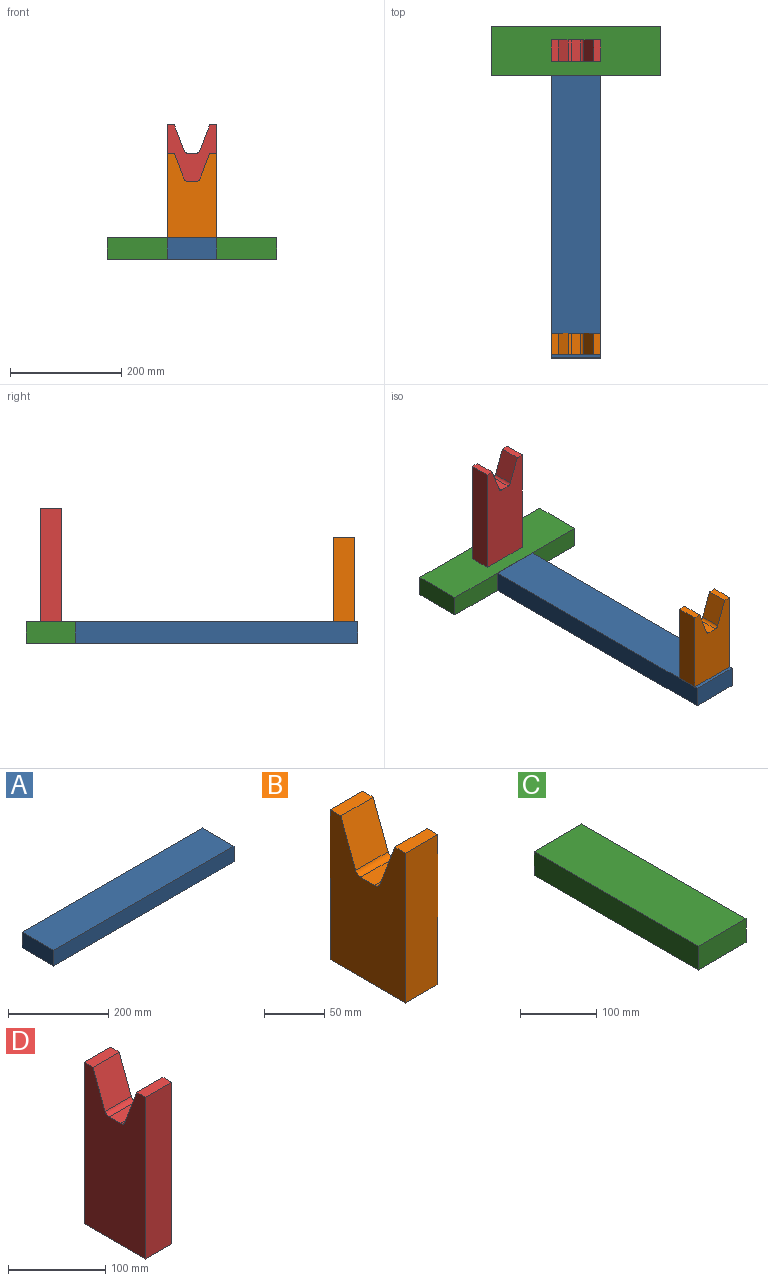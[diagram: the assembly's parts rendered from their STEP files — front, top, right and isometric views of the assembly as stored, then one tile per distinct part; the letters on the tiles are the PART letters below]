
ASSEMBLY  parts=4 mates=3
PART A: 6 faces, bbox 508x88.9x38.1 mm
  f0: plane 508x38.1mm, normal (0,-1,0), area 19354.8mm2, adj f1,f3,f4,f5
  f1: plane 508x88.9mm, normal (0,0,-1), area 45161.2mm2, adj f0,f2,f4,f5
  f2: plane 508x38.1mm, normal (0,1,0), area 19354.8mm2, adj f1,f3,f4,f5
  f3: plane 508x88.9mm, normal (0,0,1), area 45161.2mm2, adj f0,f2,f4,f5
  f4: plane 88.9x38.1mm, normal (1,0,0), area 3387.1mm2, adj f0,f1,f2,f3
  f5: plane 88.9x38.1mm, normal (-1,0,0), area 3387.1mm2, adj f0,f1,f2,f3
PART B: 12 faces, bbox 38.1x88.9x152.4 mm
  f0: plane 38.1x12.7mm, normal (0,0,1), area 483.9mm2, adj f1,f9,f10,f11
  f1: plane 152.4x38.1mm, normal (0,-1,0), area 5806.4mm2, adj f0,f2,f10,f11
  f2: plane 88.9x38.1mm, normal (0,0,-1), area 3387.1mm2, adj f1,f3,f10,f11
  f3: plane 152.4x38.1mm, normal (0,1,0), area 5806.4mm2, adj f2,f4,f10,f11
  f4: plane 38.1x12.7mm, normal (0,0,1), area 483.9mm2, adj f3,f5,f10,f11
  f5: plane 46.68x38.1mm, normal (0,-0.94,0.35), area 1899.4mm2, adj f4,f6,f10,f11
  f6: cylinder r=6.35mm len=38.1mm, axis (-1,0,0), area 293.2mm2, adj f5,f7,f10,f11
  f7: plane 38.1x16.6mm, normal (0,0,1), area 632.4mm2, adj f6,f8,f10,f11
  f8: cylinder r=6.35mm len=38.1mm, axis (-1,0,0), area 293.2mm2, adj f7,f9,f10,f11
  f9: plane 46.68x38.1mm, normal (0,0.94,0.35), area 1899.4mm2, adj f0,f8,f10,f11
  f10: plane 152.4x88.9mm, normal (1,0,0), area 11297.3mm2, adj f0,f1,f2,f3,f4,f5,f6,f7
  f11: plane 152.4x88.9mm, normal (-1,0,0), area 11297.3mm2, adj f0,f1,f2,f3,f4,f5,f6,f7
PART C: 6 faces, bbox 88.9x304.8x38.1 mm
  f0: plane 304.8x88.9mm, normal (0,0,1), area 27096.7mm2, adj f1,f3,f4,f5
  f1: plane 304.8x38.1mm, normal (-1,0,0), area 11612.9mm2, adj f0,f2,f4,f5
  f2: plane 304.8x88.9mm, normal (0,0,-1), area 27096.7mm2, adj f1,f3,f4,f5
  f3: plane 304.8x38.1mm, normal (1,0,0), area 11612.9mm2, adj f0,f2,f4,f5
  f4: plane 88.9x38.1mm, normal (0,-1,0), area 3387.1mm2, adj f0,f1,f2,f3
  f5: plane 88.9x38.1mm, normal (0,1,0), area 3387.1mm2, adj f0,f1,f2,f3
PART D: 12 faces, bbox 38.1x88.9x203.2 mm
  f0: plane 38.1x12.7mm, normal (0,0,1), area 483.9mm2, adj f1,f9,f10,f11
  f1: plane 203.2x38.1mm, normal (0,-1,0), area 7741.9mm2, adj f0,f2,f10,f11
  f2: plane 88.9x38.1mm, normal (0,0,-1), area 3387.1mm2, adj f1,f3,f10,f11
  f3: plane 203.2x38.1mm, normal (0,1,0), area 7741.9mm2, adj f2,f4,f10,f11
  f4: plane 38.1x12.7mm, normal (0,0,1), area 483.9mm2, adj f3,f5,f10,f11
  f5: plane 46.68x38.1mm, normal (0,-0.94,0.35), area 1899.4mm2, adj f4,f6,f10,f11
  f6: cylinder r=6.35mm len=38.1mm, axis (-1,0,0), area 293.2mm2, adj f5,f7,f10,f11
  f7: plane 38.1x16.6mm, normal (0,0,1), area 632.4mm2, adj f6,f8,f10,f11
  f8: cylinder r=6.35mm len=38.1mm, axis (-1,0,0), area 293.2mm2, adj f7,f9,f10,f11
  f9: plane 46.68x38.1mm, normal (0,0.94,0.35), area 1899.4mm2, adj f0,f8,f10,f11
  f10: plane 203.2x88.9mm, normal (1,0,0), area 15813.4mm2, adj f0,f1,f2,f3,f4,f5,f6,f7
  f11: plane 203.2x88.9mm, normal (-1,0,0), area 15813.4mm2, adj f0,f1,f2,f3,f4,f5,f6,f7
PLACE A rot(axis=(0,0,-1),90deg) t=(59.83,60.6,-177.78)mm
PLACE B rot(axis=(0,0,1),90deg) t=(123.24,-441.05,-30.48)mm
PLACE C rot(axis=(0.71,0.71,0),180deg) t=(189.14,147.2,-141.44)mm
PLACE D rot(axis=(0,0,1),90deg) t=(2.77,86,-70.42)mm
MATE fastened C.f1 <-> A.f5  axis (0,-1,0) through (36.74,60.6,-158.73)mm
MATE fastened C.f2 <-> D.f2  axis (0,0,1) through (36.74,105.05,-139.68)mm
MATE fastened B.f2 <-> A.f3  axis (0,0,-1) through (36.74,-422,-139.68)mm
